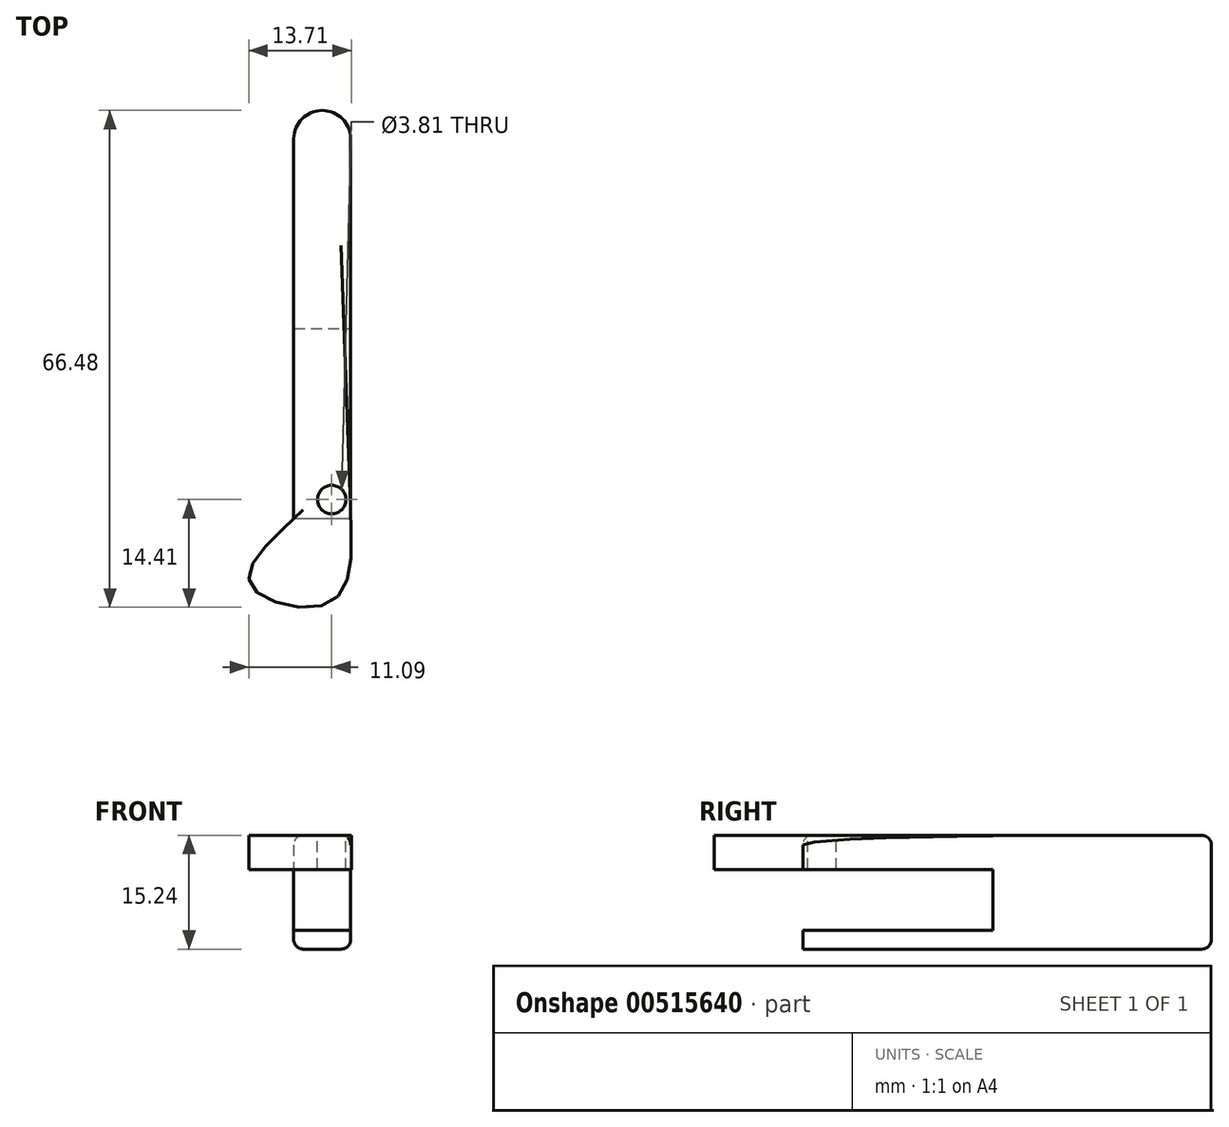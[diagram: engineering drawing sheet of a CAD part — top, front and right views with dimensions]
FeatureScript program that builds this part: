
annotation { "Feature Type Name" : "Feature", "Feature Type Description" : "" }
export const myFeature = defineFeature(function(context is Context, id is Id, definition is map)
    precondition{}
    {
        {
            var Q0;
            Q0=qCreatedBy(makeId("Top.planeOp"),FACE);
            var sketch = newSketch(context, id + "F0", { "sketchPlane" : qUnion([Q0])});
            skFitSpline(sketch, "E0", {"points": [v(0, 0) * mm, v(-5.74, -8.9) * mm, v(4.78, -11.24) * mm, v(7.62, 0) * mm], "startDerivative": vector(-32.16, -29.94) * mm, "endDerivative": vector(-1.47, 42.28) * mm});
            skLineSegment(sketch, "E1.left", {"start": v(0, 0) * mm, "end": v(0, 0) * mm});
            skLineSegment(sketch, "E1.right", {"start": v(7.62, 0) * mm, "end": v(7.62, 0) * mm});
            skLineSegment(sketch, "E2", {"start": v(7.62, 0) * mm, "end": v(7.62, 50.8) * mm});
            skLineSegment(sketch, "E3", {"start": v(7.62, 50.8) * mm, "end": v(0, 50.8) * mm});
            skLineSegment(sketch, "E4", {"start": v(0, 50.8) * mm, "end": v(0, 0) * mm});
            skArc(sketch, "E5", {"start": v(0, 50.8) * mm, "mid": v(3.8, 54.61) * mm, "end": v(7.62, 50.8) * mm});
            skSolve(sketch);
        }
        {
            var Q0;
            Q0 = qSketchRegion(id + "F0", true);
            extrude(context, id + "F1", {"entities" : qUnion([Q0]), "depth" : 4.57 * mm, "offsetDistance" : 25.4 * mm});
        }
        {
            var Q0;
            Q0=makeQuery(id+"F1.opExtrude","CAP_FACE",FACE,{"disambiguationData":[OSD([sQuery(id+"F0.wireOp",EDGE,"E0"),sQuery(id+"F0.wireOp",EDGE,"E2"),sQuery(id+"F0.wireOp",EDGE,"E3"),sQuery(id+"F0.wireOp",EDGE,"E4")])],"isStart":false});
            var sketch = newSketch(context, id + "F2", { "sketchPlane" : qUnion([Q0])});
            skPoint(sketch, "E6", {"position": v(5.08, 2.54) * mm});
            skSolve(sketch);
        }
        {
            var Q0;
            Q0=sQuery(id+"F2.wireOp",VERTEX,"E6");
            var Q1;
            Q1=makeQuery(id+"F1.opExtrude","SWEPT_BODY",BODY,{"disambiguationData":[OSD([sQuery(id+"F0.wireOp",EDGE,"E0"),sQuery(id+"F0.wireOp",EDGE,"E2"),sQuery(id+"F0.wireOp",EDGE,"E3"),sQuery(id+"F0.wireOp",EDGE,"E4")])]});
            hole(context, id + "F3", {"style" : HoleStyle.SIMPLE, "endStyle" : HoleEndStyle.THROUGH, "holeDiameter" : 3.8 * mm, "isTappedThrough" : true, "tappedDepth" : 12.7 * mm, "tapClearance" : 3, "locations" : qUnion([Q0]), "scope" : qUnion([Q1])});
        }
        {
            var Q0;
            Q0=makeQuery(id+"F1.opExtrude","CAP_FACE",FACE,{"disambiguationData":[OSD([sQuery(id+"F0.wireOp",EDGE,"E0"),sQuery(id+"F0.wireOp",EDGE,"E2"),sQuery(id+"F0.wireOp",EDGE,"E3"),sQuery(id+"F0.wireOp",EDGE,"E4")])],"isStart":true});
            var sketch = newSketch(context, id + "F4", { "sketchPlane" : qUnion([Q0])});
            skLineSegment(sketch, "E7.bottom", {"start": v(0, -50.8) * mm, "end": v(7.62, -50.8) * mm});
            skLineSegment(sketch, "E7.top", {"start": v(0, -25.4) * mm, "end": v(7.62, -25.4) * mm});
            skLineSegment(sketch, "E7.left", {"start": v(0, -50.8) * mm, "end": v(0, -25.4) * mm});
            skLineSegment(sketch, "E7.right", {"start": v(7.62, -50.8) * mm, "end": v(7.62, -25.4) * mm});
            skArc(sketch, "E8", {"start": v(0, -50.8) * mm, "mid": v(3.81, -54.61) * mm, "end": v(7.62, -50.8) * mm});
            skSolve(sketch);
        }
        {
            var Q0;
            Q0 = qSketchRegion(id + "F4", true);
            extrude(context, id + "F5", {"entities" : qUnion([Q0]), "operationType" : NewBodyOperationType.ADD, "depth" : 8.13 * mm, "offsetDistance" : 25.4 * mm});
        }
        {
            var Q0;
            Q0=makeQuery(id+"F5.opExtrude","CAP_FACE",FACE,{"disambiguationData":[OSD([sQuery(id+"F4.wireOp",EDGE,"E7.bottom"),sQuery(id+"F4.wireOp",EDGE,"E7.top"),sQuery(id+"F4.wireOp",EDGE,"E7.left"),sQuery(id+"F4.wireOp",EDGE,"E7.right")])],"isStart":false});
            var sketch = newSketch(context, id + "F6", { "sketchPlane" : qUnion([Q0])});
            skLineSegment(sketch, "E9.bottom", {"start": v(0, -50.8) * mm, "end": v(7.62, -50.8) * mm});
            skLineSegment(sketch, "E9.top", {"start": v(0, 0) * mm, "end": v(7.62, 0) * mm});
            skLineSegment(sketch, "E9.left", {"start": v(0, -50.8) * mm, "end": v(0, 0) * mm});
            skLineSegment(sketch, "E9.right", {"start": v(7.62, -50.8) * mm, "end": v(7.62, 0) * mm});
            skArc(sketch, "E10", {"start": v(7.62, -50.8) * mm, "mid": v(3.81, -54.6) * mm, "end": v(0, -50.8) * mm});
            skSolve(sketch);
        }
        {
            var Q0;
            Q0 = qSketchRegion(id + "F6", true);
            extrude(context, id + "F7", {"entities" : qUnion([Q0]), "operationType" : NewBodyOperationType.ADD, "depth" : 2.54 * mm, "offsetDistance" : 25.4 * mm});
        }
        {
            var Q0;
            Q0=makeQuery(id+"F7.opExtrude","CAP_EDGE",EDGE,{"disambiguationData":[OSD([sQuery(id+"F6.wireOp",EDGE,"E9.right")])],"isStart":false});
            var Q1;
            Q1=makeQuery(id+"F7.opExtrude","CAP_EDGE",EDGE,{"disambiguationData":[OSD([sQuery(id+"F6.wireOp",EDGE,"E9.left")])],"isStart":false});
            var Q2;
            Q2=makeQuery(id+"F1.opExtrude","CAP_EDGE",EDGE,{"disambiguationData":[OSD([sQuery(id+"F0.wireOp",EDGE,"E4")])],"isStart":false});
            fillet(context, id + "F8", {"entities" : qUnion([Q0, Q1, Q2]), "radius" : 1.27 * mm, "tangentPropagation" : true, "allowEdgeOverflow" : false});
        }
    });
